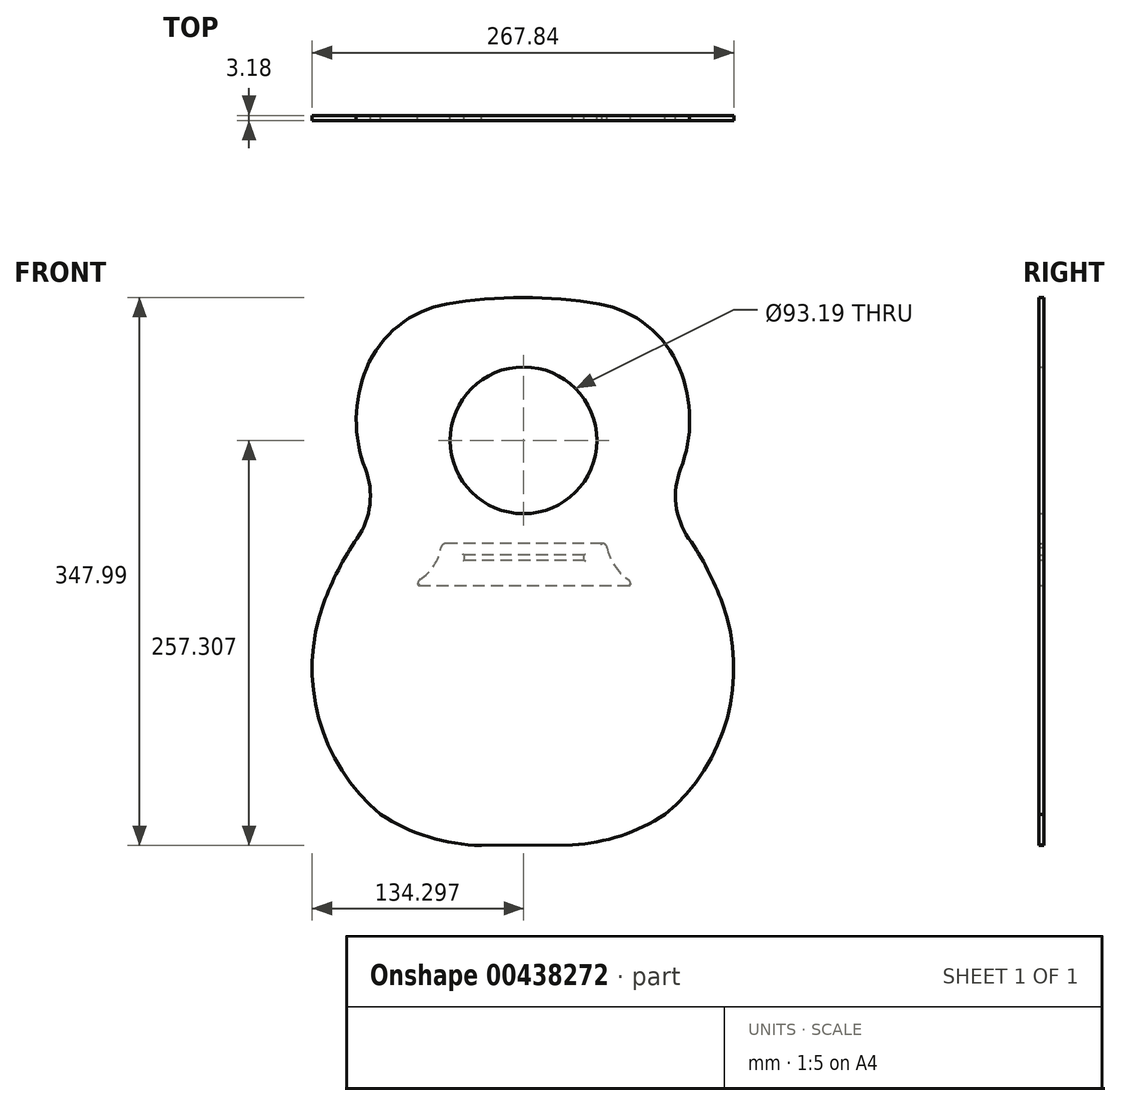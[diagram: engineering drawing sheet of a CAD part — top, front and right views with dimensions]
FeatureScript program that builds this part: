
annotation { "Feature Type Name" : "Feature", "Feature Type Description" : "" }
export const myFeature = defineFeature(function(context is Context, id is Id, definition is map)
    precondition{}
    {
        {
            var Q0;
            Q0=qCreatedBy(makeId("Front.planeOp"),FACE);
            var sketch = newSketch(context, id + "F0", { "sketchPlane" : qUnion([Q0])});
            skLineSegment(sketch, "E0", {"start": v(0, 0) * mm, "end": v(0, 212.2) * mm, "construction": true});
            skLineSegment(sketch, "E1", {"start": v(0, 212.2) * mm, "end": v(0, 174.35) * mm, "construction": true});
            skLineSegment(sketch, "E2", {"start": v(0, -273.08) * mm, "end": v(0, 0) * mm, "construction": true});
            skLineSegment(sketch, "E3", {"start": v(0, 174.35) * mm, "end": v(0, 0) * mm, "construction": true});
            skArc(sketch, "E4", {"start": v(-48.46, 167.48) * mm, "mid": v(-79.17, 153.61) * mm, "end": v(-99.38, 126.64) * mm});
            skArc(sketch, "E5", {"start": v(-99.38, 126.64) * mm, "mid": v(-105.89, 94.74) * mm, "end": v(-100.1, 62.71) * mm});
            skArc(sketch, "E6", {"start": v(-100.1, 62.71) * mm, "mid": v(-97.23, 40.09) * mm, "end": v(-105.26, 18.75) * mm});
            skArc(sketch, "E7", {"start": v(-105.26, 18.75) * mm, "mid": v(-117.25, -1.3) * mm, "end": v(-126.63, -22.7) * mm});
            skArc(sketch, "E8", {"start": v(-126.63, -22.7) * mm, "mid": v(-129.73, -95.42) * mm, "end": v(-90.32, -156.63) * mm});
            skCircle(sketch, "E9", {"center": v(0.38, 80.93) * mm, "radius": 46.6 * mm});
            skArc(sketch, "E10.MirrorCS", {"start": v(48.46, 167.48) * mm, "mid": v(79.17, 153.61) * mm, "end": v(99.38, 126.64) * mm});
            skArc(sketch, "E11.MirrorCS", {"start": v(105.26, 18.75) * mm, "mid": v(117.25, -1.3) * mm, "end": v(126.63, -22.7) * mm});
            skArc(sketch, "E12.MirrorCS", {"start": v(100.1, 62.71) * mm, "mid": v(97.23, 40.09) * mm, "end": v(105.26, 18.75) * mm});
            skArc(sketch, "E13.MirrorCS", {"start": v(126.63, -22.7) * mm, "mid": v(129.73, -95.42) * mm, "end": v(90.32, -156.63) * mm});
            skArc(sketch, "E14.MirrorCS", {"start": v(99.38, 126.64) * mm, "mid": v(105.89, 94.74) * mm, "end": v(100.1, 62.71) * mm});
            skArc(sketch, "E15", {"start": v(48.46, 167.48) * mm, "mid": v(30.3, 170) * mm, "end": v(12.03, 171.36) * mm});
            skArc(sketch, "E16", {"start": v(-12.8, 171.32) * mm, "mid": v(-30.68, 169.96) * mm, "end": v(-48.46, 167.48) * mm});
            skArc(sketch, "E17", {"start": v(12.03, 171.36) * mm, "mid": v(-0.38, 171.61) * mm, "end": v(-12.8, 171.32) * mm});
            skArc(sketch, "E18", {"start": v(-90.32, -156.63) * mm, "mid": v(-59.76, -171.09) * mm, "end": v(-26.37, -176.38) * mm});
            skArc(sketch, "E19", {"start": v(31.43, -176.06) * mm, "mid": v(62.14, -170.18) * mm, "end": v(90.32, -156.63) * mm});
            skLineSegment(sketch, "E20", {"start": v(-26.37, -176.38) * mm, "end": v(31.43, -176.06) * mm});
            skSolve(sketch);
        }
        {
            var Q0;
            Q0=makeQuery(id+"F0.imprint","IMPRINT",FACE,{"disambiguationData":[TD([[makeQuery(id+"F0.imprint","IMPRINT",EDGE,{"derivedFrom":sQuery(id+"F0.wireOp",EDGE,"E4")}),1.0]])]});
            extrude(context, id + "F1", {"entities" : qUnion([Q0]), "depth" : 3.17 * mm});
        }
        {
            var Q0;
            Q0=qCreatedBy(makeId("Front.planeOp"),FACE);
            var sketch = newSketch(context, id + "F2", { "sketchPlane" : qUnion([Q0])});
            skLineSegment(sketch, "E21.top", {"start": v(50.33, 15.48) * mm, "end": v(-48.84, 15.48) * mm});
            skPoint(sketch, "E21.middle", {"position": v(0.74, 4.98) * mm});
            skArc(sketch, "E22", {"start": v(-65.4, -7.46) * mm, "mid": v(-56.58, 1.32) * mm, "end": v(-51.96, 12.86) * mm});
            skLineSegment(sketch, "E23", {"start": v(-66.83, -10.11) * mm, "end": v(-66.83, -10.6) * mm});
            skLineSegment(sketch, "E24", {"start": v(-66.32, -11.12) * mm, "end": v(0.74, -11.12) * mm});
            skPoint(sketch, "E25.visualSharp", {"position": v(-51.6, 15.48) * mm});
            skArc(sketch, "E25.filletArc", {"start": v(-48.84, 15.48) * mm, "mid": v(-50.87, 14.74) * mm, "end": v(-51.96, 12.86) * mm});
            skPoint(sketch, "E26.visualSharp", {"position": v(-66.83, -8.34) * mm});
            skArc(sketch, "E26.filletArc", {"start": v(-65.4, -7.46) * mm, "mid": v(-66.44, -8.6) * mm, "end": v(-66.83, -10.11) * mm});
            skPoint(sketch, "E27.visualSharp", {"position": v(-66.83, -11.12) * mm});
            skArc(sketch, "E27.filletArc", {"start": v(-66.83, -10.6) * mm, "mid": v(-66.68, -10.97) * mm, "end": v(-66.32, -11.12) * mm});
            skLineSegment(sketch, "E28.MirrorCS", {"start": v(68.31, -10.11) * mm, "end": v(68.31, -10.6) * mm});
            skLineSegment(sketch, "E29.MirrorCS", {"start": v(67.8, -11.12) * mm, "end": v(0.74, -11.12) * mm});
            skArc(sketch, "E30.MirrorCS", {"start": v(68.31, -10.6) * mm, "mid": v(68.16, -10.97) * mm, "end": v(67.8, -11.12) * mm});
            skArc(sketch, "E31.MirrorCS", {"start": v(50.33, 15.47) * mm, "mid": v(52.33, 14.77) * mm, "end": v(53.43, 12.95) * mm});
            skArc(sketch, "E32.MirrorCS", {"start": v(66.88, -7.46) * mm, "mid": v(67.93, -8.6) * mm, "end": v(68.31, -10.11) * mm});
            skPoint(sketch, "E33.MirrorP", {"position": v(68.31, -11.12) * mm});
            skArc(sketch, "E34.MirrorCS", {"start": v(66.88, -7.46) * mm, "mid": v(58.04, 1.36) * mm, "end": v(53.43, 12.95) * mm});
            skPoint(sketch, "E35.MirrorP", {"position": v(53.08, 15.66) * mm});
            skPoint(sketch, "E36.MirrorP", {"position": v(68.31, -8.34) * mm});
            skLineSegment(sketch, "E37", {"start": v(0.74, 4.98) * mm, "end": v(-37.38, 4.98) * mm});
            skLineSegment(sketch, "E38", {"start": v(-37.38, 4.98) * mm, "end": v(0.74, 4.98) * mm});
            skLineSegment(sketch, "E39", {"start": v(0.74, 4.98) * mm, "end": v(38.85, 4.98) * mm});
            skLineSegment(sketch, "E40", {"start": v(38.85, 4.98) * mm, "end": v(38.85, 8.03) * mm});
            skLineSegment(sketch, "E41", {"start": v(38.85, 8.03) * mm, "end": v(-37.38, 8.03) * mm});
            skLineSegment(sketch, "E42", {"start": v(-37.38, 8.03) * mm, "end": v(-37.38, 4.98) * mm});
            skLineSegment(sketch, "E43", {"start": v(50.33, 15.48) * mm, "end": v(50.33, 15.47) * mm});
            skSolve(sketch);
        }
        {
            var Q0;
            Q0=makeQuery(id+"F2.imprint","IMPRINT",FACE,{"disambiguationData":[TD([[makeQuery(id+"F2.imprint","IMPRINT",EDGE,{"derivedFrom":sQuery(id+"F2.wireOp",EDGE,"E21.top")}),1.0]])]});
            extrude(context, id + "F3", {"entities" : qUnion([Q0]), "depth" : 3.17 * mm});
        }
        {
            var Q0;
            Q0=makeQuery(id+"F3.opExtrude","CAP_EDGE",EDGE,{"disambiguationData":[OSD([sQuery(id+"F2.wireOp",EDGE,"E24"),sQuery(id+"F2.wireOp",EDGE,"E29.MirrorCS")])],"isStart":false});
            var Q1;
            Q1=makeQuery(id+"F3.opExtrude","SWEPT_FACE",FACE,{"disambiguationData":[OSD([sQuery(id+"F2.wireOp",EDGE,"E22")])]});
            var Q2;
            Q2=makeQuery(id+"F3.opExtrude","CAP_FACE",FACE,{"disambiguationData":[OSD([sQuery(id+"F2.wireOp",EDGE,"E21.top"),sQuery(id+"F2.wireOp",EDGE,"E22"),sQuery(id+"F2.wireOp",EDGE,"E23"),sQuery(id+"F2.wireOp",EDGE,"E24"),sQuery(id+"F2.wireOp",EDGE,"E25.filletArc"),sQuery(id+"F2.wireOp",EDGE,"E26.filletArc"),sQuery(id+"F2.wireOp",EDGE,"E27.filletArc"),sQuery(id+"F2.wireOp",EDGE,"E28.MirrorCS"),sQuery(id+"F2.wireOp",EDGE,"E29.MirrorCS"),sQuery(id+"F2.wireOp",EDGE,"E30.MirrorCS"),sQuery(id+"F2.wireOp",EDGE,"E31.MirrorCS"),sQuery(id+"F2.wireOp",EDGE,"E32.MirrorCS"),sQuery(id+"F2.wireOp",EDGE,"E34.MirrorCS"),sQuery(id+"F2.wireOp",EDGE,"E38"),sQuery(id+"F2.wireOp",EDGE,"E39"),sQuery(id+"F2.wireOp",EDGE,"E40"),sQuery(id+"F2.wireOp",EDGE,"E41"),sQuery(id+"F2.wireOp",EDGE,"E42"),sQuery(id+"F2.wireOp",EDGE,"E43")])],"isStart":false});
            fillet(context, id + "F4", {"entities" : qUnion([Q0, Q1, Q2]), "radius" : 0.76 * mm, "tangentPropagation" : true, "allowEdgeOverflow" : false});
        }
    });
